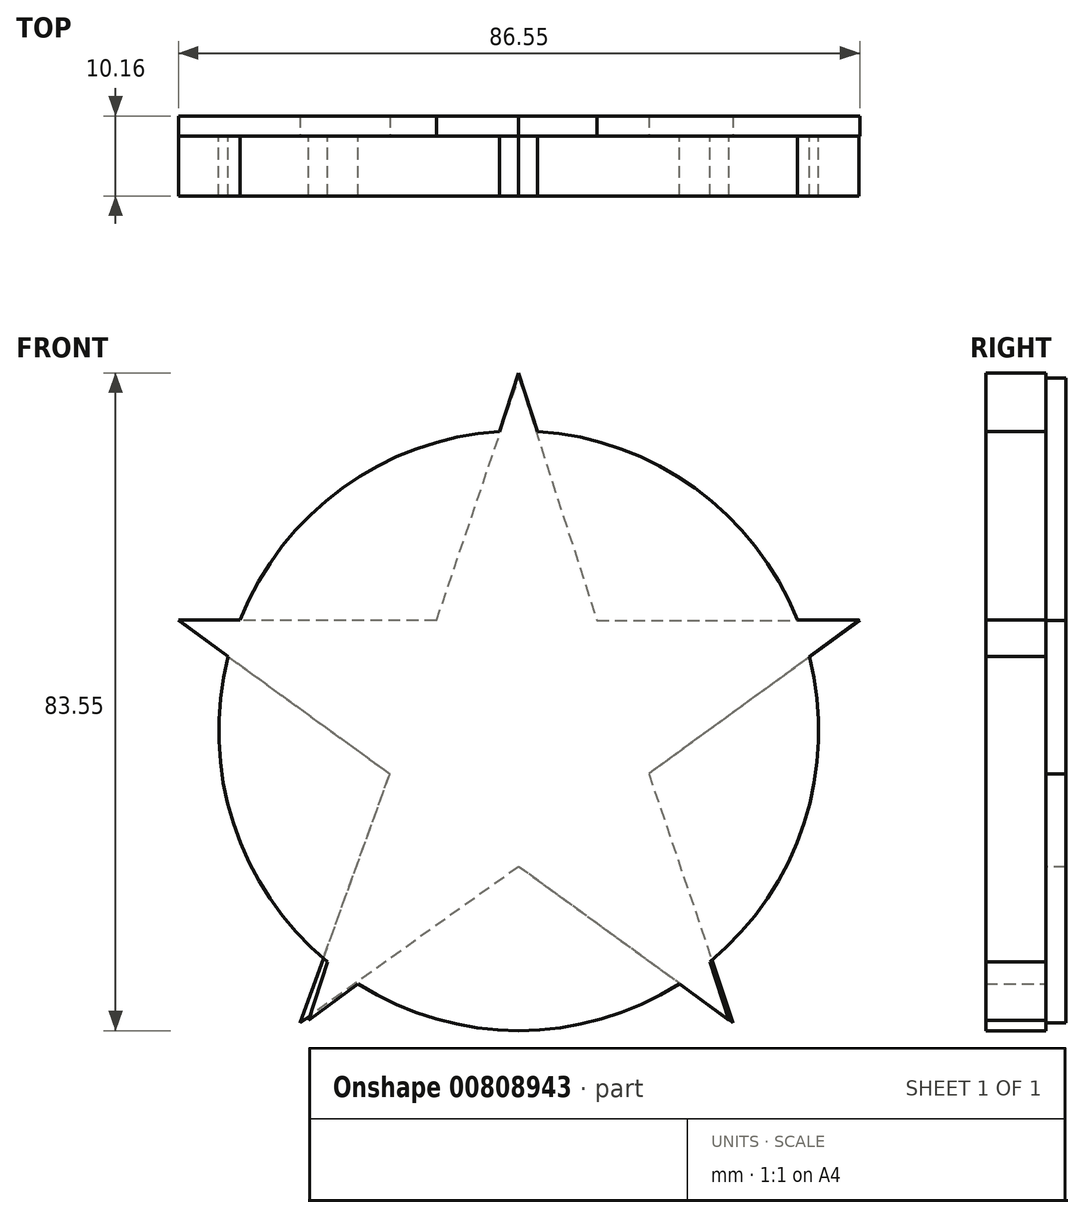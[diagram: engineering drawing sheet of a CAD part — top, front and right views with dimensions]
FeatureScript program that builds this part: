
annotation { "Feature Type Name" : "Feature", "Feature Type Description" : "" }
export const myFeature = defineFeature(function(context is Context, id is Id, definition is map)
    precondition{}
    {
        {
            var Q0;
            Q0=qCreatedBy(makeId("Front.planeOp"),FACE);
            var sketch = newSketch(context, id + "F0", { "sketchPlane" : qUnion([Q0])});
            skCircle(sketch, "E0", {"center": v(0, 0) * mm, "radius": 38.1 * mm});
            skSolve(sketch);
        }
        {
            var Q0;
            Q0 = qSketchRegion(id + "F0", true);
            extrude(context, id + "F1", {"entities" : qUnion([Q0]), "depth" : 7.62 * mm, "offsetDistance" : 25.4 * mm});
        }
        {
            var Q0;
            Q0=qCreatedBy(makeId("Front.planeOp"),FACE);
            var sketch = newSketch(context, id + "F2", { "sketchPlane" : qUnion([Q0])});
            skCircle(sketch, "E1.cCircle", {"center": v(0, 0) * mm, "radius": 14.04 * mm, "construction": true});
            skLineSegment(sketch, "E1.0", {"start": v(10.2, 14.04) * mm, "end": v(16.51, -5.36) * mm});
            skLineSegment(sketch, "E1.1", {"start": v(16.51, -5.36) * mm, "end": v(0, -17.36) * mm});
            skLineSegment(sketch, "E1.2", {"start": v(0, -17.36) * mm, "end": v(-16.51, -5.36) * mm});
            skLineSegment(sketch, "E1.3", {"start": v(-16.51, -5.36) * mm, "end": v(-10.2, 14.04) * mm});
            skLineSegment(sketch, "E1.4", {"start": v(-10.2, 14.04) * mm, "end": v(10.2, 14.04) * mm});
            skPoint(sketch, "E1.0.midPoint", {"position": v(13.36, 4.34) * mm});
            skLineSegment(sketch, "E2", {"start": v(-10.2, 14.04) * mm, "end": v(0, 45.45) * mm});
            skLineSegment(sketch, "E3", {"start": v(0, 45.45) * mm, "end": v(10.2, 14.04) * mm});
            skLineSegment(sketch, "E4", {"start": v(10.2, 14.04) * mm, "end": v(43.22, 14.04) * mm});
            skLineSegment(sketch, "E5", {"start": v(43.22, 14.04) * mm, "end": v(16.51, -5.36) * mm});
            skLineSegment(sketch, "E6", {"start": v(16.51, -5.36) * mm, "end": v(26.71, -36.77) * mm});
            skLineSegment(sketch, "E7", {"start": v(26.71, -36.77) * mm, "end": v(0, -17.36) * mm});
            skLineSegment(sketch, "E8", {"start": v(0, -17.36) * mm, "end": v(-26.71, -36.77) * mm});
            skLineSegment(sketch, "E9", {"start": v(-26.71, -36.77) * mm, "end": v(-16.51, -5.36) * mm});
            skLineSegment(sketch, "E10", {"start": v(-16.51, -5.36) * mm, "end": v(-43.22, 14.04) * mm});
            skLineSegment(sketch, "E11", {"start": v(-43.22, 14.04) * mm, "end": v(-10.2, 14.04) * mm});
            skSolve(sketch);
        }
        {
            var Q0;
            Q0 = qSketchRegion(id + "F2", true);
            extrude(context, id + "F3", {"entities" : qUnion([Q0]), "operationType" : NewBodyOperationType.ADD, "depth" : 7.62 * mm, "offsetDistance" : 25.4 * mm});
        }
        {
            var Q0;
            Q0=makeQuery(id+"F2.imprint","IMPRINT",FACE,{"disambiguationData":[TD([[makeQuery(id+"F2.imprint","IMPRINT",EDGE,{"derivedFrom":sQuery(id+"F2.wireOp",EDGE,"E1.0")}),-1.0]])]});
            var sketch = newSketch(context, id + "F4", { "sketchPlane" : qUnion([Q0])});
            skLineSegment(sketch, "E12", {"start": v(9.95, 13.99) * mm, "end": v(-10.44, 13.99) * mm});
            skLineSegment(sketch, "E13", {"start": v(-10.44, 13.99) * mm, "end": v(-16.36, -5.46) * mm});
            skLineSegment(sketch, "E14", {"start": v(-16.36, -5.46) * mm, "end": v(0, -17.27) * mm});
            skLineSegment(sketch, "E15", {"start": v(0, -17.27) * mm, "end": v(16.53, -5.46) * mm});
            skLineSegment(sketch, "E16", {"start": v(16.53, -5.46) * mm, "end": v(9.95, 13.99) * mm});
            skLineSegment(sketch, "E17", {"start": v(-10.44, 13.99) * mm, "end": v(-43.19, 13.99) * mm});
            skLineSegment(sketch, "E18", {"start": v(-43.19, 13.99) * mm, "end": v(-16.36, -5.46) * mm});
            skLineSegment(sketch, "E19", {"start": v(-10.44, 13.99) * mm, "end": v(0, 44.83) * mm});
            skLineSegment(sketch, "E20", {"start": v(0, 44.83) * mm, "end": v(9.95, 13.99) * mm});
            skLineSegment(sketch, "E21", {"start": v(9.95, 13.99) * mm, "end": v(43.33, 13.99) * mm});
            skLineSegment(sketch, "E22", {"start": v(43.33, 13.99) * mm, "end": v(16.53, -5.46) * mm});
            skLineSegment(sketch, "E23", {"start": v(16.53, -5.46) * mm, "end": v(27.24, -37.08) * mm});
            skLineSegment(sketch, "E24", {"start": v(27.24, -37.08) * mm, "end": v(0, -17.27) * mm});
            skLineSegment(sketch, "E25", {"start": v(0, -17.27) * mm, "end": v(-27.76, -37.08) * mm});
            skLineSegment(sketch, "E26", {"start": v(-27.76, -37.08) * mm, "end": v(-16.36, -5.46) * mm});
            skSolve(sketch);
        }
        {
            var Q0;
            Q0 = qSketchRegion(id + "F4", true);
            extrude(context, id + "F5", {"entities" : qUnion([Q0]), "operationType" : NewBodyOperationType.ADD, "oppositeDirection" : true, "depth" : 2.54 * mm, "offsetDistance" : 25.4 * mm});
        }
    });
